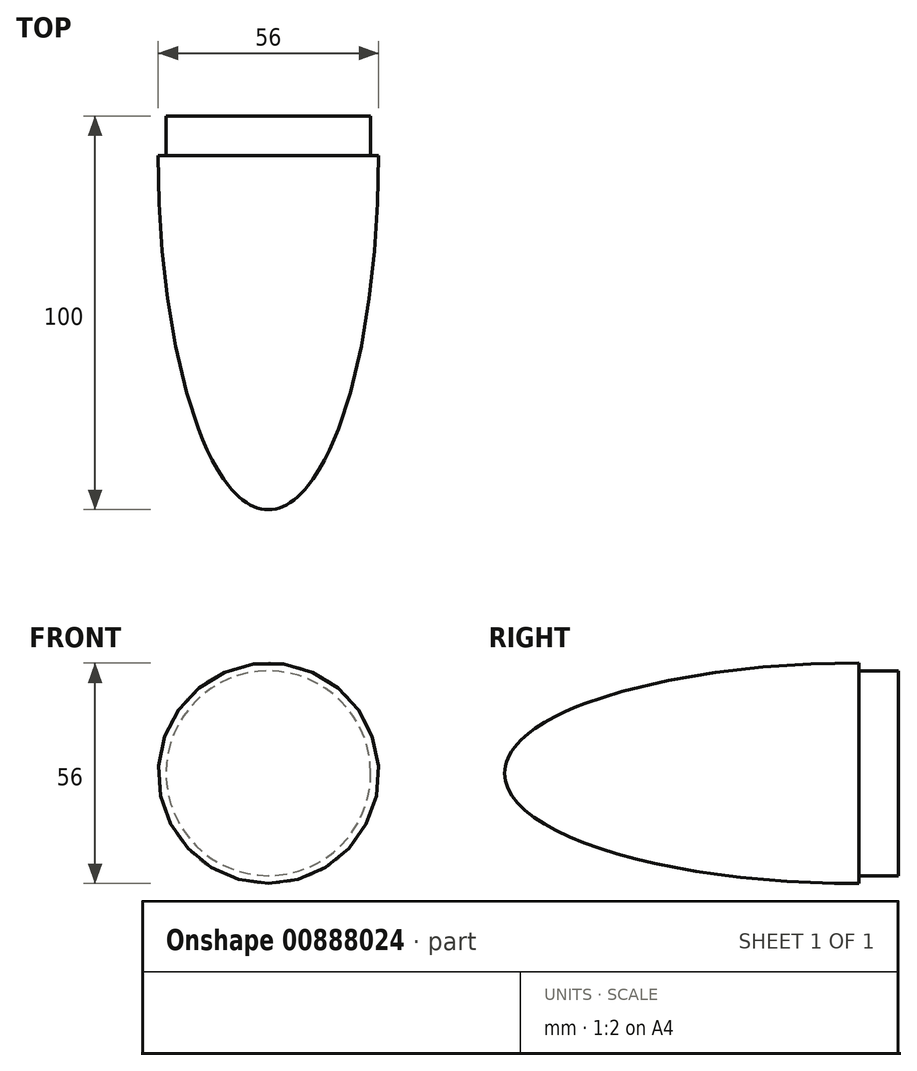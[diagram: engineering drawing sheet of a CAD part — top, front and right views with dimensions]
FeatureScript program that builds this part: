
annotation { "Feature Type Name" : "Feature", "Feature Type Description" : "" }
export const myFeature = defineFeature(function(context is Context, id is Id, definition is map)
    precondition{}
    {
        {
            var Q0;
            Q0=qCreatedBy(makeId("Right.planeOp"),FACE);
            var sketch = newSketch(context, id + "F0", { "sketchPlane" : qUnion([Q0])});
            skLineSegment(sketch, "E0.bottom", {"start": v(0, 0) * mm, "end": v(10, 0) * mm});
            skLineSegment(sketch, "E0.top", {"start": v(0, -26) * mm, "end": v(10, -26) * mm});
            skLineSegment(sketch, "E0.left", {"start": v(0, 0) * mm, "end": v(0, -26) * mm});
            skLineSegment(sketch, "E0.right", {"start": v(10, 0) * mm, "end": v(10, -26) * mm});
            skLineSegment(sketch, "E1.bottom", {"start": v(0, 0) * mm, "end": v(-90, 0) * mm});
            skLineSegment(sketch, "E1.top", {"start": v(0, -28) * mm, "end": v(-90, -28) * mm});
            skLineSegment(sketch, "E1.left", {"start": v(0, 0) * mm, "end": v(0, -28) * mm});
            skLineSegment(sketch, "E1.right", {"start": v(-90, 0) * mm, "end": v(-90, -28) * mm});
            skEllipse(sketch, "E2", {"center": v(0, 0) * mm, "majorRadius": 90 * mm, "minorRadius": 28 * mm, "majorAxis": v(-1, 0)});
            skSolve(sketch);
        }
        {
            var Q0;
            {var subQ0=sQuery(id+"F0.wireOp",EDGE,"E1.bottom");Q0=makeQuery(id+"F0.imprint","IMPRINT",FACE,{"disambiguationData":[TD([[makeQuery(id+"F0.imprint","IMPRINT",EDGE,{"derivedFrom":subQ0}),1.0]])]});}
            var Q1;
            {var subQ0=sQuery(id+"F0.wireOp",EDGE,"E0.bottom");Q1=makeQuery(id+"F0.imprint","IMPRINT",FACE,{"disambiguationData":[TD([[makeQuery(id+"F0.imprint","IMPRINT",EDGE,{"derivedFrom":subQ0}),-1.0]])]});}
            var Q2;
            Q2=sQuery(id+"F0.wireOp",EDGE,"E1.bottom");
            revolve(context, id + "F1", {"entities" : qUnion([Q0, Q1]), "axis" : qUnion([Q2]), "revolveType" : RevolveType.FULL});
        }
    });
